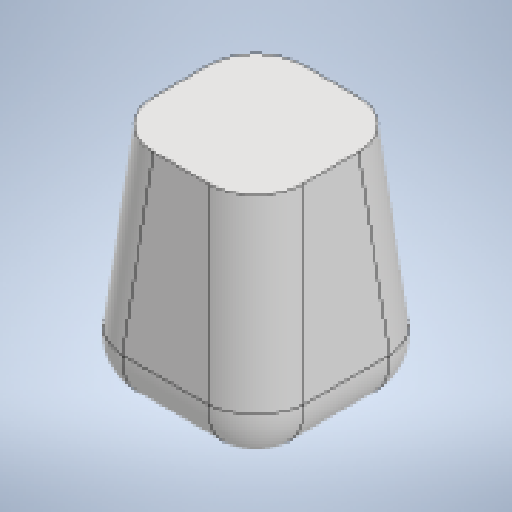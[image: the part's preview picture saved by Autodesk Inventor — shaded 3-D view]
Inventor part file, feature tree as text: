
AUTODESK INVENTOR PART (.ipt)
format: ipt  version: 2025 (Build 290162010, 162A)  size: 152,064 bytes
history: native  units: mm
features: extrude x1, fillet x1, sketch x1
ambient origin geometry x8: Origin, YZ Plane, XZ Plane, XY Plane, X Axis, Y Axis, Z Axis, Center Point
bodies: Solid1 (feature_tree)
feature tree (3):
  extrude  "Extrusion1"  Depth=250.0mm
  fillet  "Fillet1"  Radius=1200.0mm
  sketch  "Sketch1"  dims[d0=1000.0mm d1=1000.0mm d2=1200.0mm d3=-0.872665mm d4=250.0mm]
